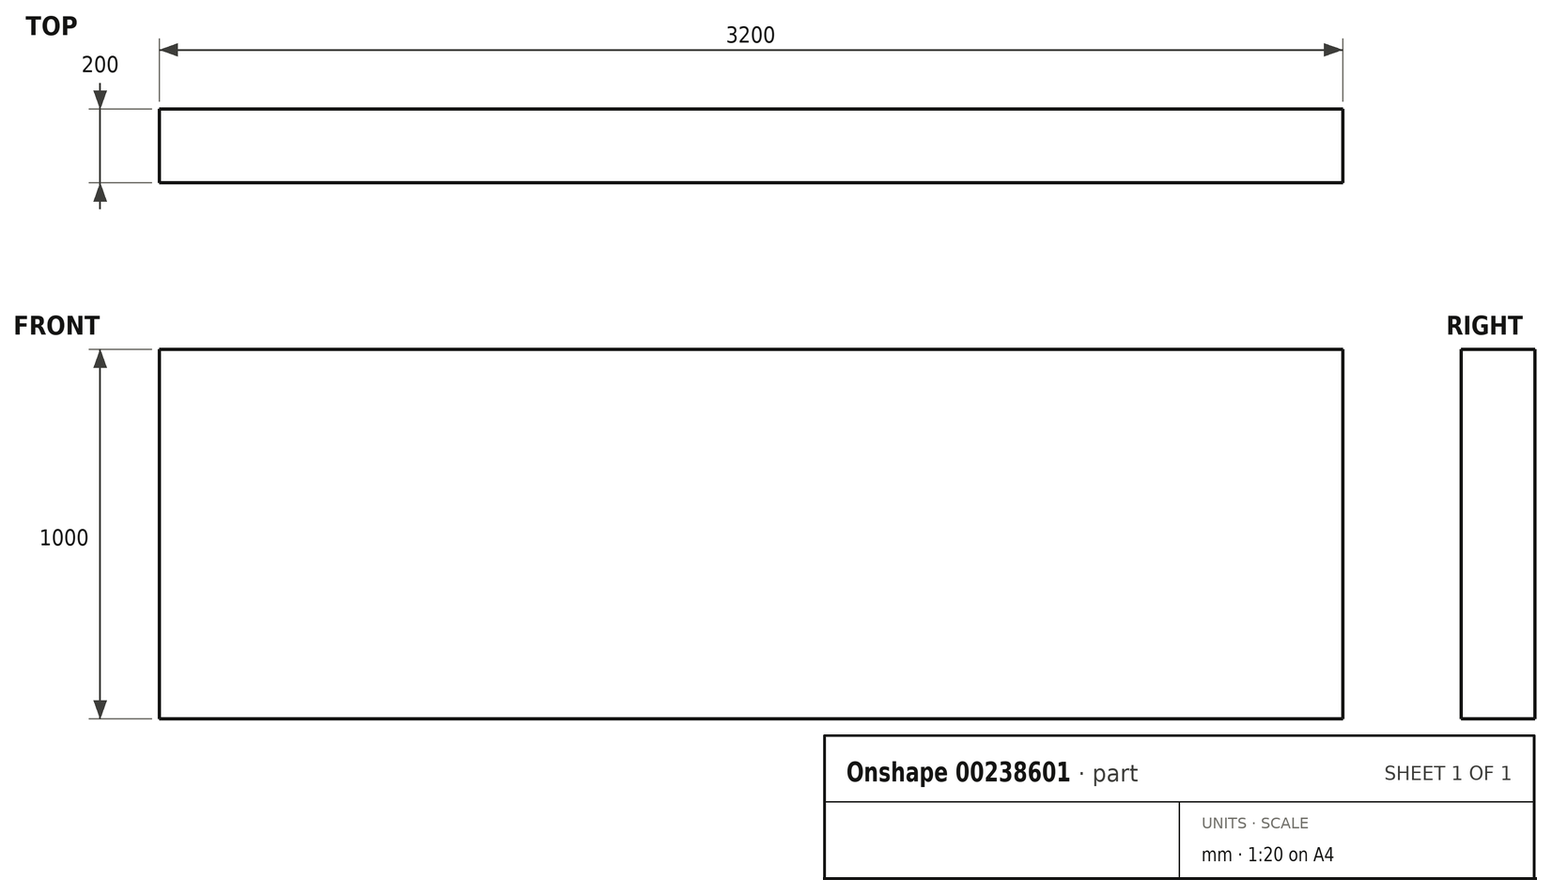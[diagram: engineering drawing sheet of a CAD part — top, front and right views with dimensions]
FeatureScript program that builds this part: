
annotation { "Feature Type Name" : "Feature", "Feature Type Description" : "" }
export const myFeature = defineFeature(function(context is Context, id is Id, definition is map)
    precondition{}
    {
        {
            var Q0;
            Q0=qCreatedBy(makeId("Front.planeOp"),FACE);
            var sketch = newSketch(context, id + "F0", { "sketchPlane" : qUnion([Q0])});
            skLineSegment(sketch, "E0.bottom", {"start": v(0, 0) * mm, "end": v(-3200, 0) * mm});
            skLineSegment(sketch, "E0.top", {"start": v(0, 1000) * mm, "end": v(-3200, 1000) * mm});
            skLineSegment(sketch, "E0.left", {"start": v(0, 0) * mm, "end": v(0, 1000) * mm});
            skLineSegment(sketch, "E0.right", {"start": v(-3200, 0) * mm, "end": v(-3200, 1000) * mm});
            skSolve(sketch);
        }
        {
            var Q0;
            Q0=makeQuery(id+"F0.imprint","IMPRINT",FACE,{"disambiguationData":[TD([[makeQuery(id+"F0.imprint","IMPRINT",EDGE,{"derivedFrom":sQuery(id+"F0.wireOp",EDGE,"E0.bottom")}),-1.0]])]});
            extrude(context, id + "F1", {"entities" : qUnion([Q0]), "depth" : 200 * mm});
        }
    });
